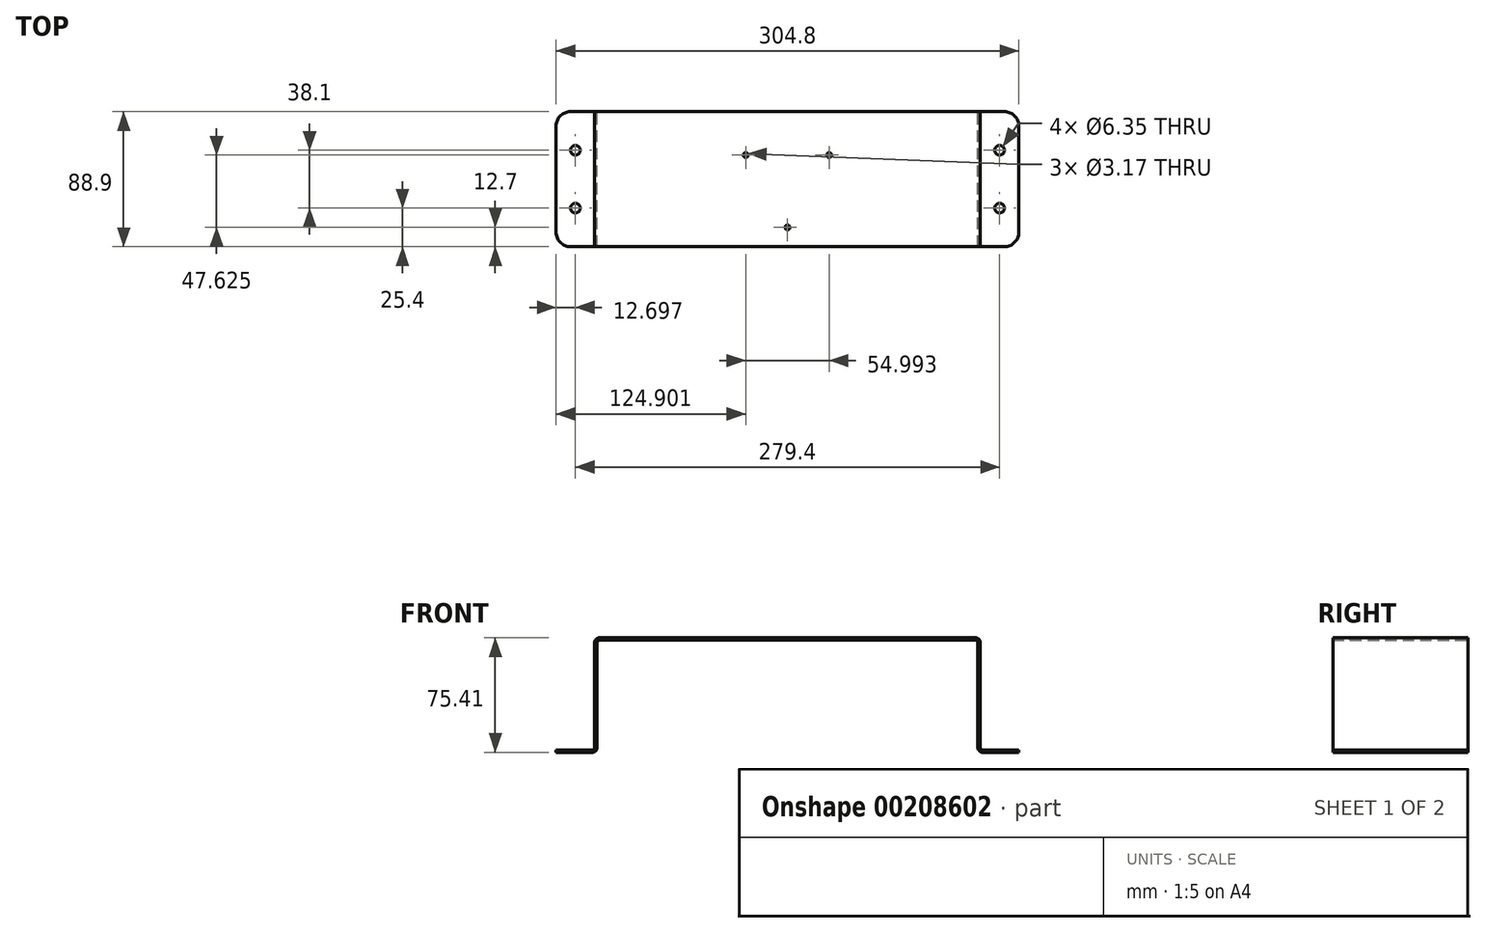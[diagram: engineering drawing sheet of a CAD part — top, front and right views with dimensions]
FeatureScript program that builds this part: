
annotation { "Feature Type Name" : "Feature", "Feature Type Description" : "" }
export const myFeature = defineFeature(function(context is Context, id is Id, definition is map)
    precondition{}
    {
        {
            var Q0;
            Q0=qCreatedBy(makeId("Front.planeOp"),FACE);
            var sketch = newSketch(context, id + "F0", { "sketchPlane" : qUnion([Q0])});
            skLineSegment(sketch, "E0", {"start": v(-1.59, 0) * mm, "end": v(-125.41, 0) * mm});
            skLineSegment(sketch, "E1", {"start": v(0, -1.59) * mm, "end": v(0, -70.64) * mm});
            skPoint(sketch, "E2.visualSharp", {"position": v(0, 0) * mm});
            skArc(sketch, "E2.filletArc", {"start": v(0, -1.59) * mm, "mid": v(-0.46, -0.46) * mm, "end": v(-1.59, 0) * mm});
            skLineSegment(sketch, "E3.0", {"start": v(-1.59, 1.59) * mm, "end": v(-125.41, 1.59) * mm});
            skArc(sketch, "E3.1", {"start": v(1.59, -1.59) * mm, "mid": v(0.66, 0.66) * mm, "end": v(-1.59, 1.59) * mm});
            skLineSegment(sketch, "E3.2", {"start": v(1.59, -1.59) * mm, "end": v(1.59, -70.64) * mm});
            skLineSegment(sketch, "E4", {"start": v(-125.41, 1.59) * mm, "end": v(-125.41, 0) * mm, "construction": true});
            skLineSegment(sketch, "E5", {"start": v(3.18, -72.23) * mm, "end": v(26.99, -72.23) * mm});
            skPoint(sketch, "E6.visualSharp", {"position": v(1.59, -72.23) * mm});
            skArc(sketch, "E6.filletArc", {"start": v(1.59, -70.64) * mm, "mid": v(2.05, -71.77) * mm, "end": v(3.18, -72.23) * mm});
            skLineSegment(sketch, "E7.0", {"start": v(3.18, -73.82) * mm, "end": v(26.99, -73.82) * mm});
            skArc(sketch, "E7.1", {"start": v(0, -70.64) * mm, "mid": v(0.93, -72.89) * mm, "end": v(3.18, -73.82) * mm});
            skLineSegment(sketch, "E8", {"start": v(26.99, -72.23) * mm, "end": v(26.99, -73.82) * mm});
            skLineSegment(sketch, "E9.MirrorCS", {"start": v(-249.24, 1.59) * mm, "end": v(-125.41, 1.59) * mm});
            skLineSegment(sketch, "E10.MirrorCS", {"start": v(-249.24, 0) * mm, "end": v(-125.41, 0) * mm});
            skArc(sketch, "E11.MirrorCS", {"start": v(-252.41, -1.59) * mm, "mid": v(-251.48, 0.66) * mm, "end": v(-249.24, 1.59) * mm});
            skArc(sketch, "E12.MirrorCS", {"start": v(-250.83, -1.59) * mm, "mid": v(-250.36, -0.46) * mm, "end": v(-249.24, 0) * mm});
            skLineSegment(sketch, "E13.MirrorCS", {"start": v(-250.83, -1.59) * mm, "end": v(-250.83, -70.64) * mm});
            skLineSegment(sketch, "E14.MirrorCS", {"start": v(-252.41, -1.59) * mm, "end": v(-252.41, -70.64) * mm});
            skArc(sketch, "E15.MirrorCS", {"start": v(-250.83, -70.64) * mm, "mid": v(-251.75, -72.89) * mm, "end": v(-254, -73.82) * mm});
            skArc(sketch, "E16.MirrorCS", {"start": v(-252.41, -70.64) * mm, "mid": v(-252.88, -71.77) * mm, "end": v(-254, -72.23) * mm});
            skLineSegment(sketch, "E17.MirrorCS", {"start": v(-254, -72.23) * mm, "end": v(-277.81, -72.23) * mm});
            skLineSegment(sketch, "E18.MirrorCS", {"start": v(-254, -73.82) * mm, "end": v(-277.81, -73.82) * mm});
            skLineSegment(sketch, "E19.MirrorCS", {"start": v(-277.81, -72.23) * mm, "end": v(-277.81, -73.82) * mm});
            skSolve(sketch);
        }
        {
            var Q0;
            Q0=qSketchRegion(id+"F0",true);
            extrude(context, id + "F1", {"entities" : qUnion([Q0]), "endBound" : BoundingType.SYMMETRIC, "depth" : 88.9 * mm});
        }
        {
            var Q0;
            Q0=makeQuery(id+"F1.opExtrude","SWEPT_FACE",FACE,{"disambiguationData":[OSD([sQuery(id+"F0.wireOp",EDGE,"E3.0")])]});
            var sketch = newSketch(context, id + "F2", { "sketchPlane" : qUnion([Q0])});
            skCircle(sketch, "E20", {"center": v(14.29, 19.05) * mm, "radius": 3.18 * mm});
            skCircle(sketch, "E21", {"center": v(14.29, -19.05) * mm, "radius": 3.18 * mm});
            skCircle(sketch, "E22", {"center": v(-125.41, 0) * mm, "radius": 31.75 * mm, "construction": true});
            skCircle(sketch, "E23", {"center": v(-125.41, -31.75) * mm, "radius": 1.59 * mm});
            skCircle(sketch, "E24.1.0", {"center": v(-97.92, 15.88) * mm, "radius": 1.59 * mm});
            skCircle(sketch, "E24.2.0", {"center": v(-152.9, 15.88) * mm, "radius": 1.59 * mm});
            skLineSegment(sketch, "E25", {"start": v(-125.41, 44.45) * mm, "end": v(-125.41, 76.94) * mm, "construction": true});
            skCircle(sketch, "E26.MirrorC", {"center": v(-265.11, 19.05) * mm, "radius": 3.18 * mm});
            skCircle(sketch, "E27.MirrorC", {"center": v(-265.11, -19.05) * mm, "radius": 3.18 * mm});
            skSolve(sketch);
        }
        {
            var Q0;
            Q0=qSketchRegion(id+"F2",true);
            extrude(context, id + "F3", {"entities" : qUnion([Q0]), "operationType" : NewBodyOperationType.REMOVE, "endBound" : BoundingType.THROUGH_ALL, "oppositeDirection" : true, "depth" : 25.4 * mm});
        }
        {
            var Q0;
            Q0=makeQuery(id+"F1.opExtrude","CAP_EDGE",EDGE,{"disambiguationData":[OSD([sQuery(id+"F0.wireOp",EDGE,"E4")])],"isStart":false});
            var Q1;
            Q1=makeQuery(id+"F1.opExtrude","CAP_EDGE",EDGE,{"disambiguationData":[OSD([sQuery(id+"F0.wireOp",EDGE,"E4")])],"isStart":true});
            var Q2;
            Q2=makeQuery(id+"F1.opExtrude","CAP_EDGE",EDGE,{"disambiguationData":[OSD([sQuery(id+"F0.wireOp",EDGE,"E8")])],"isStart":true});
            var Q3;
            Q3=makeQuery(id+"F1.opExtrude","CAP_EDGE",EDGE,{"disambiguationData":[OSD([sQuery(id+"F0.wireOp",EDGE,"E8")])],"isStart":false});
            var Q4;
            Q4=makeQuery(id+"F1.opExtrude","CAP_EDGE",EDGE,{"disambiguationData":[OSD([sQuery(id+"F0.wireOp",EDGE,"E19.MirrorCS")])],"isStart":false});
            var Q5;
            Q5=makeQuery(id+"F1.opExtrude","CAP_EDGE",EDGE,{"disambiguationData":[OSD([sQuery(id+"F0.wireOp",EDGE,"E19.MirrorCS")])],"isStart":true});
            fillet(context, id + "F4", {"entities" : qUnion([Q0, Q1, Q2, Q3, Q4, Q5]), "radius" : 9.52 * mm, "tangentPropagation" : true, "allowEdgeOverflow" : false});
        }
    });
